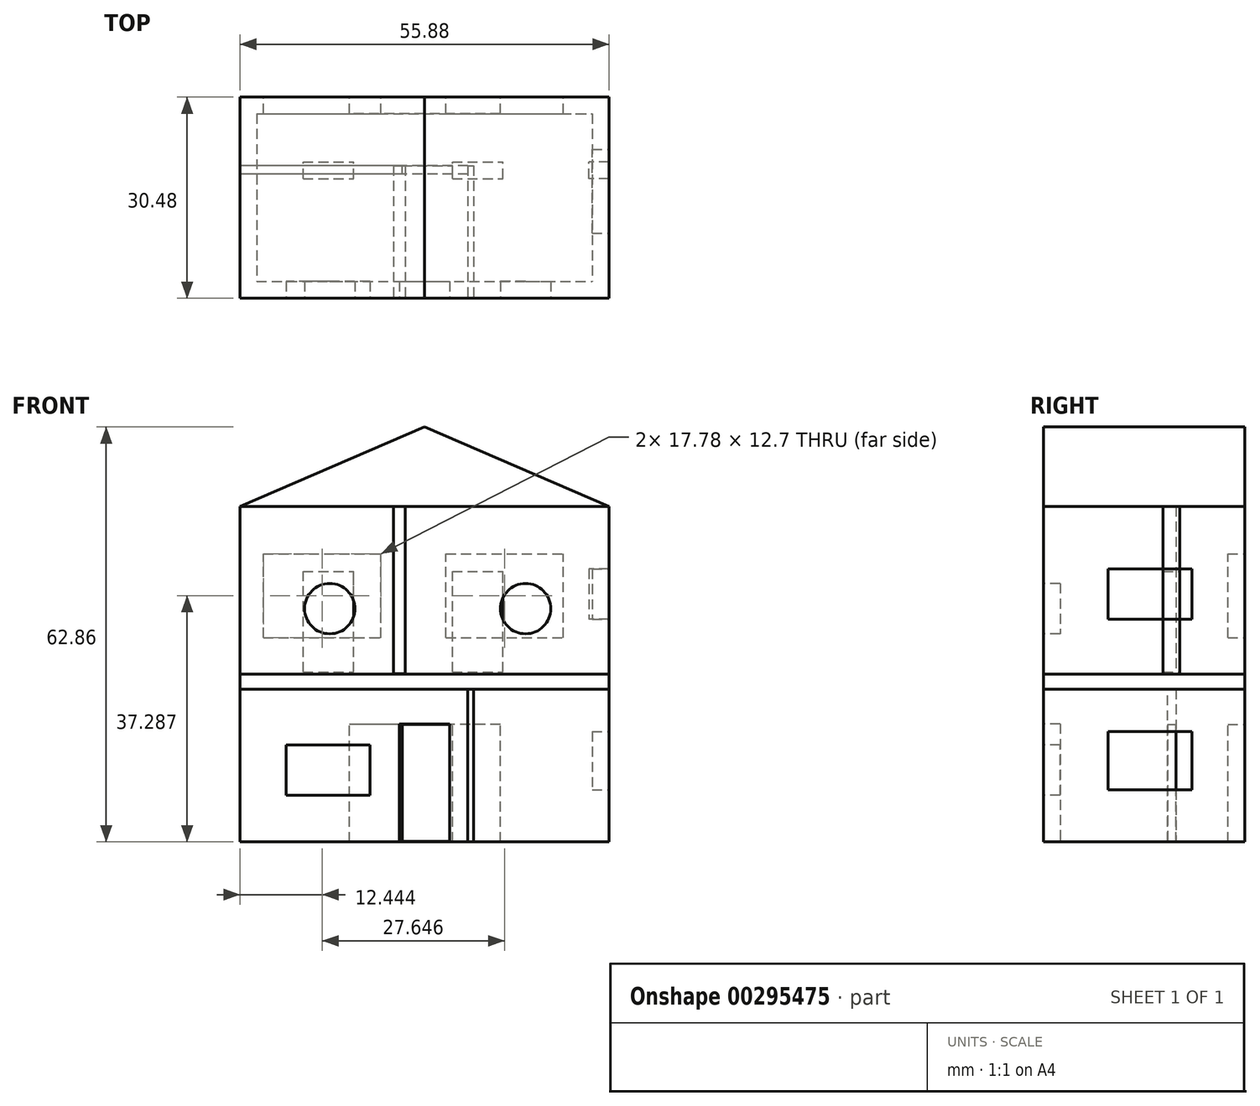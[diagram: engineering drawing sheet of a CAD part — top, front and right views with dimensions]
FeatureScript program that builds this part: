
annotation { "Feature Type Name" : "Feature", "Feature Type Description" : "" }
export const myFeature = defineFeature(function(context is Context, id is Id, definition is map)
    precondition{}
    {
        {
            var Q0;
            Q0=qCreatedBy(makeId("Top.planeOp"),FACE);
            var sketch = newSketch(context, id + "F0", { "sketchPlane" : qUnion([Q0])});
            skLineSegment(sketch, "E0.bottom", {"start": v(-64.52, 37.25) * mm, "end": v(-13.72, 37.25) * mm});
            skLineSegment(sketch, "E0.top", {"start": v(-64.52, 11.85) * mm, "end": v(-13.72, 11.85) * mm});
            skLineSegment(sketch, "E0.left", {"start": v(-64.52, 37.25) * mm, "end": v(-64.52, 11.85) * mm});
            skLineSegment(sketch, "E0.right", {"start": v(-13.72, 37.25) * mm, "end": v(-13.72, 11.85) * mm});
            skPoint(sketch, "E0.middle", {"position": v(-39.12, 24.55) * mm});
            skLineSegment(sketch, "E1.bottom", {"start": v(-67.06, 39.79) * mm, "end": v(-11.18, 39.79) * mm});
            skLineSegment(sketch, "E1.top", {"start": v(-67.06, 9.3) * mm, "end": v(-11.18, 9.3) * mm});
            skLineSegment(sketch, "E1.left", {"start": v(-67.06, 39.79) * mm, "end": v(-67.06, 9.3) * mm});
            skLineSegment(sketch, "E1.right", {"start": v(-11.18, 39.79) * mm, "end": v(-11.18, 9.3) * mm});
            skSolve(sketch);
        }
        {
            var Q0;
            Q0=makeQuery(id+"F0.imprint","IMPRINT",FACE,{"disambiguationData":[TD([[makeQuery(id+"F0.imprint","IMPRINT",EDGE,{"derivedFrom":sQuery(id+"F0.wireOp",EDGE,"E0.bottom")}),1.0]])]});
            extrude(context, id + "F1", {"entities" : qUnion([Q0]), "depth" : 50.8 * mm});
        }
        {
            var Q0;
            Q0=makeQuery(id+"F1.opExtrude","SWEPT_FACE",FACE,{"disambiguationData":[OSD([sQuery(id+"F0.wireOp",EDGE,"E1.top")])]});
            var sketch = newSketch(context, id + "F2", { "sketchPlane" : qUnion([Q0])});
            skCircle(sketch, "E2", {"center": v(-23.81, 35.33) * mm, "radius": 3.81 * mm});
            skCircle(sketch, "E3", {"center": v(-53.47, 35.33) * mm, "radius": 3.81 * mm});
            skPoint(sketch, "E4", {"position": v(-39.12, 0) * mm});
            skLineSegment(sketch, "E5.bottom", {"start": v(-60.1, 14.67) * mm, "end": v(-47.4, 14.67) * mm});
            skLineSegment(sketch, "E5.top", {"start": v(-60.1, 7.05) * mm, "end": v(-47.4, 7.05) * mm});
            skLineSegment(sketch, "E5.left", {"start": v(-60.1, 14.67) * mm, "end": v(-60.1, 7.05) * mm});
            skLineSegment(sketch, "E5.right", {"start": v(-47.4, 14.67) * mm, "end": v(-47.4, 7.05) * mm});
            skLineSegment(sketch, "E6.bottom", {"start": v(-35.31, 0.08) * mm, "end": v(-42.93, 0.08) * mm});
            skLineSegment(sketch, "E6.top", {"start": v(-35.31, 17.86) * mm, "end": v(-42.93, 17.86) * mm});
            skLineSegment(sketch, "E6.left", {"start": v(-35.31, 0.08) * mm, "end": v(-35.31, 17.86) * mm});
            skLineSegment(sketch, "E6.right", {"start": v(-42.93, 0.08) * mm, "end": v(-42.93, 17.86) * mm});
            skPoint(sketch, "E6.middle", {"position": v(-39.12, 8.97) * mm});
            skLineSegment(sketch, "E7", {"start": v(-67.06, 50.8) * mm, "end": v(-39.12, 62.86) * mm});
            skLineSegment(sketch, "E8", {"start": v(-39.12, 62.86) * mm, "end": v(-11.18, 50.8) * mm});
            skLineSegment(sketch, "E9.bottom", {"start": v(-32.6, 23.11) * mm, "end": v(-31.72, 23.11) * mm});
            skLineSegment(sketch, "E9.top", {"start": v(-32.6, 0) * mm, "end": v(-31.72, 0) * mm});
            skLineSegment(sketch, "E9.left", {"start": v(-32.6, 23.11) * mm, "end": v(-32.6, 0) * mm});
            skLineSegment(sketch, "E9.right", {"start": v(-31.72, 23.11) * mm, "end": v(-31.72, 0) * mm});
            skLineSegment(sketch, "E10.bottom", {"start": v(-43.8, 50.8) * mm, "end": v(-42.02, 50.8) * mm});
            skLineSegment(sketch, "E10.top", {"start": v(-43.8, 25.46) * mm, "end": v(-42.02, 25.46) * mm});
            skLineSegment(sketch, "E10.left", {"start": v(-43.8, 50.8) * mm, "end": v(-43.8, 25.46) * mm});
            skLineSegment(sketch, "E10.right", {"start": v(-42.02, 50.8) * mm, "end": v(-42.02, 25.46) * mm});
            skSolve(sketch);
        }
        {
            var Q0;
            Q0=makeQuery(id+"F1.opExtrude","SWEPT_FACE",FACE,{"disambiguationData":[OSD([sQuery(id+"F0.wireOp",EDGE,"E1.left")])]});
            var sketch = newSketch(context, id + "F3", { "sketchPlane" : qUnion([Q0])});
            skLineSegment(sketch, "E11", {"start": v(-39.79, 25.4) * mm, "end": v(-9.3, 25.4) * mm});
            skLineSegment(sketch, "E12", {"start": v(-39.79, 23.12) * mm, "end": v(-9.3, 23.12) * mm});
            skLineSegment(sketch, "E13", {"start": v(-29.37, 23.12) * mm, "end": v(-29.37, 0) * mm});
            skLineSegment(sketch, "E14", {"start": v(-28.13, 0) * mm, "end": v(-28.13, 23.12) * mm});
            skLineSegment(sketch, "E15.bottom", {"start": v(-29.96, 50.8) * mm, "end": v(-27.42, 50.8) * mm});
            skLineSegment(sketch, "E15.top", {"start": v(-29.96, 25.4) * mm, "end": v(-27.42, 25.4) * mm});
            skLineSegment(sketch, "E15.left", {"start": v(-29.96, 50.8) * mm, "end": v(-29.96, 25.4) * mm});
            skLineSegment(sketch, "E15.right", {"start": v(-27.42, 50.8) * mm, "end": v(-27.42, 25.4) * mm});
            skSolve(sketch);
        }
        {
            var Q0;
            {var subQ0=sQuery(id+"F3.wireOp",EDGE,"E11");Q0=makeQuery(id+"F3.imprint","IMPRINT",FACE,{"disambiguationData":[TD([[makeQuery(id+"F3.imprint","IMPRINT",EDGE,{"derivedFrom":subQ0}),-1.0]])]});}
            extrude(context, id + "F4", {"entities" : qUnion([Q0]), "oppositeDirection" : true, "depth" : 55.88 * mm});
        }
        {
            var Q0;
            {var subQ0=sQuery(id+"F3.wireOp",EDGE,"E13");Q0=makeQuery(id+"F3.imprint","IMPRINT",FACE,{"disambiguationData":[TD([[makeQuery(id+"F3.imprint","IMPRINT",EDGE,{"derivedFrom":subQ0}),1.0]])]});}
            extrude(context, id + "F5", {"entities" : qUnion([Q0]), "oppositeDirection" : true, "depth" : 34.5 * mm});
        }
        {
            var Q0;
            Q0=makeQuery(id+"F2.imprint","IMPRINT",FACE,{"disambiguationData":[TD([[makeQuery(id+"F2.imprint","IMPRINT",EDGE,{"derivedFrom":sQuery(id+"F2.wireOp",EDGE,"E9.bottom")}),-1.0]])]});
            var Q1;
            Q1=makeQuery(id+"F2.imprint","IMPRINT",FACE,{"disambiguationData":[TD([[makeQuery(id+"F2.imprint","IMPRINT",EDGE,{"derivedFrom":sQuery(id+"F2.wireOp",EDGE,"E10.bottom")}),-1.0]])]});
            extrude(context, id + "F6", {"entities" : qUnion([Q0, Q1]), "oppositeDirection" : true, "depth" : 20.07 * mm});
        }
        {
            var Q0;
            Q0=makeQuery(id+"F2.imprint","IMPRINT",FACE,{"disambiguationData":[TD([[makeQuery(id+"F2.imprint","IMPRINT",EDGE,{"derivedFrom":sQuery(id+"F2.wireOp",EDGE,"E3")}),1.0]])]});
            var Q1;
            Q1=makeQuery(id+"F2.imprint","IMPRINT",FACE,{"disambiguationData":[TD([[makeQuery(id+"F2.imprint","IMPRINT",EDGE,{"derivedFrom":sQuery(id+"F2.wireOp",EDGE,"E2")}),1.0]])]});
            var Q2;
            Q2=makeQuery(id+"F2.imprint","IMPRINT",FACE,{"disambiguationData":[TD([[makeQuery(id+"F2.imprint","IMPRINT",EDGE,{"derivedFrom":sQuery(id+"F2.wireOp",EDGE,"E6.bottom")}),-1.0]])]});
            var Q3;
            Q3=makeQuery(id+"F2.imprint","IMPRINT",FACE,{"disambiguationData":[TD([[makeQuery(id+"F2.imprint","IMPRINT",EDGE,{"derivedFrom":sQuery(id+"F2.wireOp",EDGE,"E5.bottom")}),-1.0]])]});
            extrude(context, id + "F7", {"entities" : qUnion([Q0, Q1, Q2, Q3]), "operationType" : NewBodyOperationType.REMOVE, "oppositeDirection" : true, "depth" : 12.7 * mm});
        }
        {
            var Q0;
            {var subQ0=sQuery(id+"F2.wireOp",EDGE,"E7");Q0=makeQuery(id+"F2.imprint","IMPRINT",FACE,{"disambiguationData":[TD([[makeQuery(id+"F2.imprint","IMPRINT",EDGE,{"derivedFrom":subQ0}),-1.0]])]});}
            var Q1;
            Q1=sQuery(id+"F2.wireOp",EDGE,"E7");
            var Q2;
            Q2=sQuery(id+"F2.wireOp",EDGE,"E8");
            extrude(context, id + "F8", {"entities" : qUnion([Q0]), "surfaceEntities" : qUnion([Q1, Q2]), "oppositeDirection" : true, "depth" : 30.48 * mm});
        }
        {
            var Q0;
            Q0=makeQuery(id+"F3.imprint","IMPRINT",FACE,{"disambiguationData":[TD([[makeQuery(id+"F3.imprint","IMPRINT",EDGE,{"derivedFrom":sQuery(id+"F3.wireOp",EDGE,"E15.bottom")}),-1.0]])]});
            extrude(context, id + "F9", {"entities" : qUnion([Q0]), "oppositeDirection" : true, "depth" : 55.88 * mm});
        }
        {
            var Q0;
            Q0=makeQuery(id+"F5.opExtrude","SWEPT_FACE",FACE,{"disambiguationData":[OSD([sQuery(id+"F3.wireOp",EDGE,"E13")])]});
            var sketch = newSketch(context, id + "F10", { "sketchPlane" : qUnion([Q0])});
            skLineSegment(sketch, "E16.bottom", {"start": v(42.5, 0) * mm, "end": v(34.89, 0) * mm});
            skLineSegment(sketch, "E16.top", {"start": v(42.5, 17.78) * mm, "end": v(34.89, 17.78) * mm});
            skLineSegment(sketch, "E16.left", {"start": v(42.5, 0) * mm, "end": v(42.5, 17.78) * mm});
            skLineSegment(sketch, "E16.right", {"start": v(34.89, 0) * mm, "end": v(34.89, 17.78) * mm});
            skLineSegment(sketch, "E17.bottom", {"start": v(34.89, 25.73) * mm, "end": v(27.27, 25.73) * mm});
            skLineSegment(sketch, "E17.top", {"start": v(34.89, 40.97) * mm, "end": v(27.27, 40.97) * mm});
            skLineSegment(sketch, "E17.left", {"start": v(34.89, 25.73) * mm, "end": v(34.89, 40.97) * mm});
            skLineSegment(sketch, "E17.right", {"start": v(27.27, 25.73) * mm, "end": v(27.27, 40.97) * mm});
            skLineSegment(sketch, "E18.bottom", {"start": v(57.47, 25.73) * mm, "end": v(49.85, 25.73) * mm});
            skLineSegment(sketch, "E18.top", {"start": v(57.47, 40.97) * mm, "end": v(49.85, 40.97) * mm});
            skLineSegment(sketch, "E18.left", {"start": v(57.47, 25.73) * mm, "end": v(57.47, 40.97) * mm});
            skLineSegment(sketch, "E18.right", {"start": v(49.85, 25.73) * mm, "end": v(49.85, 40.97) * mm});
            skSolve(sketch);
        }
        {
            var Q0;
            Q0 = qSketchRegion(id + "F10", true);
            extrude(context, id + "F11", {"entities" : qUnion([Q0]), "operationType" : NewBodyOperationType.REMOVE, "endBound" : BoundingType.SYMMETRIC, "oppositeDirection" : true, "depth" : 7.62 * mm});
        }
        {
            var Q0;
            Q0=makeQuery(id+"F1.opExtrude","SWEPT_FACE",FACE,{"disambiguationData":[OSD([sQuery(id+"F0.wireOp",EDGE,"E1.right")])]});
            var sketch = newSketch(context, id + "F12", { "sketchPlane" : qUnion([Q0])});
            skLineSegment(sketch, "E19.bottom", {"start": v(19.13, 41.34) * mm, "end": v(31.83, 41.34) * mm});
            skLineSegment(sketch, "E19.top", {"start": v(19.13, 33.72) * mm, "end": v(31.83, 33.72) * mm});
            skLineSegment(sketch, "E19.left", {"start": v(19.13, 41.34) * mm, "end": v(19.13, 33.72) * mm});
            skLineSegment(sketch, "E19.right", {"start": v(31.83, 41.34) * mm, "end": v(31.83, 33.72) * mm});
            skLineSegment(sketch, "E20.bottom", {"start": v(19.13, 16.7) * mm, "end": v(31.83, 16.7) * mm});
            skLineSegment(sketch, "E20.top", {"start": v(19.13, 7.86) * mm, "end": v(31.83, 7.86) * mm});
            skLineSegment(sketch, "E20.left", {"start": v(19.13, 16.7) * mm, "end": v(19.13, 7.86) * mm});
            skLineSegment(sketch, "E20.right", {"start": v(31.83, 16.7) * mm, "end": v(31.83, 7.86) * mm});
            skPoint(sketch, "E20.middle", {"position": v(25.48, 12.28) * mm});
            skPoint(sketch, "E20.middle.positionSnap0", {"position": v(25.48, 33.72) * mm});
            skPoint(sketch, "E20.centerSnap0", {"position": v(25.48, 33.72) * mm});
            skSolve(sketch);
        }
        {
            var Q0;
            Q0 = qSketchRegion(id + "F12", true);
            extrude(context, id + "F13", {"entities" : qUnion([Q0]), "operationType" : NewBodyOperationType.REMOVE, "oppositeDirection" : true, "depth" : 3.05 * mm});
        }
        {
            var Q0;
            Q0=makeQuery(id+"F1.opExtrude","SWEPT_FACE",FACE,{"disambiguationData":[OSD([sQuery(id+"F0.wireOp",EDGE,"E1.bottom")])]});
            var sketch = newSketch(context, id + "F14", { "sketchPlane" : qUnion([Q0])});
            skLineSegment(sketch, "E21.bottom", {"start": v(35.86, 30.94) * mm, "end": v(18.08, 30.94) * mm});
            skLineSegment(sketch, "E21.top", {"start": v(35.86, 43.64) * mm, "end": v(18.08, 43.64) * mm});
            skLineSegment(sketch, "E21.left", {"start": v(35.86, 30.94) * mm, "end": v(35.86, 43.64) * mm});
            skLineSegment(sketch, "E21.right", {"start": v(18.08, 30.94) * mm, "end": v(18.08, 43.64) * mm});
            skPoint(sketch, "E21.middle", {"position": v(26.97, 37.29) * mm});
            skLineSegment(sketch, "E22.bottom", {"start": v(63.5, 30.94) * mm, "end": v(45.73, 30.94) * mm});
            skLineSegment(sketch, "E22.top", {"start": v(63.5, 43.64) * mm, "end": v(45.73, 43.64) * mm});
            skLineSegment(sketch, "E22.left", {"start": v(63.5, 30.94) * mm, "end": v(63.5, 43.64) * mm});
            skLineSegment(sketch, "E22.right", {"start": v(45.73, 30.94) * mm, "end": v(45.73, 43.64) * mm});
            skPoint(sketch, "E22.middle", {"position": v(54.62, 37.29) * mm});
            skLineSegment(sketch, "E23.bottom", {"start": v(27.62, 0) * mm, "end": v(50.48, 0) * mm});
            skLineSegment(sketch, "E23.top", {"start": v(27.62, 17.78) * mm, "end": v(50.48, 17.78) * mm});
            skLineSegment(sketch, "E23.left", {"start": v(27.62, 0) * mm, "end": v(27.62, 17.78) * mm});
            skLineSegment(sketch, "E23.right", {"start": v(50.48, 0) * mm, "end": v(50.48, 17.78) * mm});
            skSolve(sketch);
        }
        {
            var Q0;
            Q0=makeQuery(id+"F14.imprint","IMPRINT",FACE,{"disambiguationData":[TD([[makeQuery(id+"F14.imprint","IMPRINT",EDGE,{"derivedFrom":sQuery(id+"F14.wireOp",EDGE,"E21.bottom")}),-1.0]])]});
            var Q1;
            Q1=makeQuery(id+"F14.imprint","IMPRINT",FACE,{"disambiguationData":[TD([[makeQuery(id+"F14.imprint","IMPRINT",EDGE,{"derivedFrom":sQuery(id+"F14.wireOp",EDGE,"E22.bottom")}),-1.0]])]});
            var Q2;
            Q2=makeQuery(id+"F14.imprint","IMPRINT",FACE,{"disambiguationData":[TD([[makeQuery(id+"F14.imprint","IMPRINT",EDGE,{"derivedFrom":sQuery(id+"F14.wireOp",EDGE,"E23.bottom")}),-1.0]])]});
            extrude(context, id + "F15", {"entities" : qUnion([Q0, Q1, Q2]), "operationType" : NewBodyOperationType.REMOVE, "oppositeDirection" : true, "depth" : 5.08 * mm});
        }
    });
